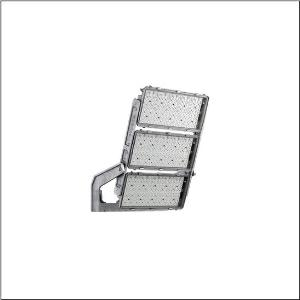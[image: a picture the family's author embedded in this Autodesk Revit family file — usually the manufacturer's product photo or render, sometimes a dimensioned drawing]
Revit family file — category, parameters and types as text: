
# Revit family: floodlight_fl_11_maxi_pro_remote___pl64_5xa779428v01aa_599d
name_source: partatom
category: Lighting Fixtures
units: mm (PartAtom-declared; Revit-internal decimal feet)

## family parameters
Cut with Voids When Loaded = No
Host = Face
Light Source = No
Part Type = Normal
Room Calculation Point = No
Round Connector Dimension = Use Diameter
Shared = No

## types (1)
- --- (1 x LED, 196240 lm, 1539.6 W, 5700K)
    Apparent Load = 1540 VA
    CIE Flux Codes = 28 79 98 100 100
    Color Rendering = 80
    Color Temperature = 5700K
    Default Elevation = 1800 mm
    Description = Floodlight FL 11  maxi  pro Remote floodlight; light control with lens of PMMA; cover panel of toughened safety glass, transparent; light distribution: PL64, asymmetric direct distribution, LEDcolour temperature: 5700K, rated luminous flux: 196.240lm, colour rendering: CRI > 80, light colour: 857; luminous efficacy: 128lm/W; brightness control: DALI 2 (1 DALI address); with terminal, 8-pole, max. 2.5mm², mains connection: 220..240V/380..400V AC, 50/60Hz, surge voltage resistance: line to ground: 10kV, dimming range 10..100%, dustproof LED module, LED unit replaceable without ESD environment, no afterglow with DALI off / DMX off command, ECG replaceable separately; 1540W floodlight with 3x LED unit of diecast aluminium, coated grey; length: 1.003mm / width: 651mm / height: 338mm; mounting bracket, of diecast aluminium, uncoated, natural, equipment: Power, protection rating (complete): IP66; insulation class (complete): insulation class I (protective earthing); certification: CE, ENEC, VDE; ball protection: ball impact resistant, impact resistance: IK07; only for outdoor installations, rated ambient temperature 10°C, permissible operating ambient temperature: -40..+30°C, permissible storage temperature: -40..+85°C; packaging unit: 1 piece

Light Distribution: PL64
    Height = 320 mm
    Lamp = 1 x LED
    Lamp Light Flux = 196240 lm
    Lamp Power = 1539.6 W
    Lamp count = 1
    Length = 1002 mm
    Luminous efficacy = 127 lm/W
    Manufacturer = Siteco
    ModVariant = No
    Model = 5XA779428V01AA
    Mounting Place = Ceiling
    Mounting Type = Surface mounted
    Number of Poles = 1
    OnlyDefault = Yes
    Power Factor = 1
    Product Name = Floodlight FL 11 maxi pro Remote | PL64
    Product group = floodlight | ceiling mounted
    ProductGroupID = 303
    Protection Class = Protection class I
    Protection Degree = IP 66
    RLX_Detail_Level = 1
    RLX_Emergency_Light_Flux = 0 lm
    RLX_Emergency_Type = 0
    RLX_Emergency_Type_DB = No
    RlxData = <blob elided: 52409 chars, md5=1b0fa2bb>
    Socket = socket
    Standby Power = 0 W
    System Light Flux = 196240 lm
    System Power = 1540 W
    Type Comments = factory setting: luminous flux: 100 % | dim-lin: 254 | 1080 mA
    Type Image = l_1006784.jpg
    URL = http://relux.com
    VarID = @adj_050639
    Voltage = 0 V
    Weight = 0.00 kg
    Width = 655 mm

## geometry (parser evidence)
native form markers: Blend x4, Sweep x12
no freeform markers — native parametric forms only
